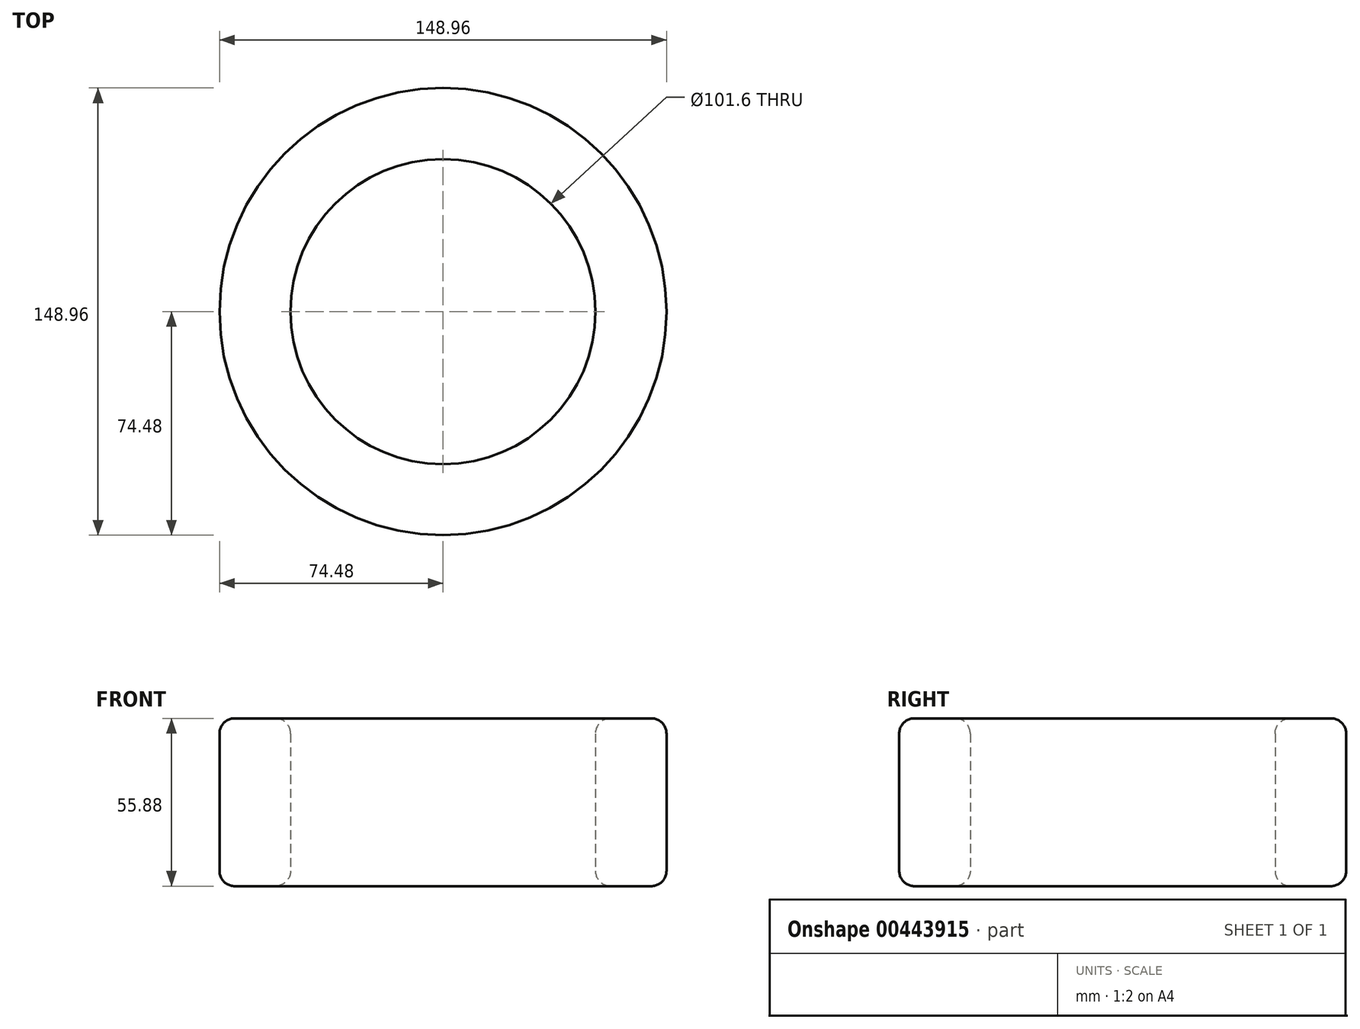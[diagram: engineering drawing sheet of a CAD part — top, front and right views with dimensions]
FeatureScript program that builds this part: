
annotation { "Feature Type Name" : "Feature", "Feature Type Description" : "" }
export const myFeature = defineFeature(function(context is Context, id is Id, definition is map)
    precondition{}
    {
        {
            var Q0;
            Q0=qCreatedBy(makeId("Top.planeOp"),FACE);
            var sketch = newSketch(context, id + "F0", { "sketchPlane" : qUnion([Q0])});
            skCircle(sketch, "E0", {"center": v(0, 0) * mm, "radius": 50.8 * mm});
            skCircle(sketch, "E1", {"center": v(0, 0) * mm, "radius": 74.48 * mm});
            skSolve(sketch);
        }
        {
            var Q0;
            Q0=qSketchRegion(id+"F0",true);
            extrude(context, id + "F1", {"entities" : qUnion([Q0]), "depth" : 55.88 * mm});
        }
        {
            var Q0;
            Q0=makeQuery(id+"F1.opExtrude","CAP_EDGE",EDGE,{"disambiguationData":[OSD([sQuery(id+"F0.wireOp",EDGE,"E1")])],"isStart":false});
            var Q1;
            Q1=makeQuery(id+"F1.opExtrude","CAP_EDGE",EDGE,{"disambiguationData":[OSD([sQuery(id+"F0.wireOp",EDGE,"E1")])],"isStart":true});
            var Q2;
            Q2=makeQuery(id+"F1.opExtrude","CAP_EDGE",EDGE,{"disambiguationData":[OSD([sQuery(id+"F0.wireOp",EDGE,"E0")])],"isStart":false});
            var Q3;
            Q3=makeQuery(id+"F1.opExtrude","CAP_EDGE",EDGE,{"disambiguationData":[OSD([sQuery(id+"F0.wireOp",EDGE,"E0")])],"isStart":true});
            fillet(context, id + "F2", {"entities" : qUnion([Q0, Q1, Q2, Q3]), "radius" : 5.08 * mm, "tangentPropagation" : true, "allowEdgeOverflow" : false});
        }
    });
